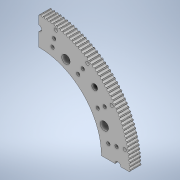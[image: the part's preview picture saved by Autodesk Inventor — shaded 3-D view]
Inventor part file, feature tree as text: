
AUTODESK INVENTOR PART (.ipt)
format: ipt  version: 2020 (Build 240168000, 168)  size: 660,992 bytes
history: native  units: in
note: dims shown in document units (in); Inventor stores cm internally (conversion verified against a paired STEP export)
features: extrude x6, sketch x6, pattern_circular x1
ambient origin geometry x8: Origin, YZ Plane, XZ Plane, XY Plane, X Axis, Y Axis, Z Axis, Center Point
bodies: Solid1 (feature_tree)
feature tree (13):
  extrude  "Extrusion1"  Depth=0.6299in TaperAngle=0.0deg
  extrude  "Extrusion2"  TaperAngle=0.0deg  [1 undecoded]
  pattern_circular  "Circular Pattern1"  Count=176 Angle=360.0deg
  extrude  "Extrusion3"  Depth=4.25in
  extrude  "Extrusion4"  Depth=0.3937in TaperAngle=360.0deg
  extrude  "Extrusion5"  Depth=4.25in
  extrude  "Extrusion6"  Depth=3.1496in TaperAngle=360.0deg
  sketch  "Sketch1"  dims[d0=10.9831in d1=0.6299in d2=0.0in]
  sketch  "Sketch2"  dims[d3=0.0607in d5=0.0in d6=0.0in d7=69.2913in d8=360.0deg]
  sketch  "Sketch3"  dims[d10=0.2031in d11=4.25in]
  sketch  "Sketch4"  dims[d12=1.1811in d14=0.5in d15=0.3937in d17=1.0in d19=6.2992in d21=360.0deg]
  sketch  "Sketch5"  dims[d23=0.5in d24=4.25in]
  sketch  "Sketch6"  dims[d25=0.0773in d26=3.1496in d28=360.0deg d30=4.735in d31=0.35in d33=0.0773in d34=3.1496in d36=360.0deg d38=0.0773in d39=0.0in d40=0.0in d41=7.5in d42=0.0in d43=0.0in d44=0.0in d45=0.0in d47=0.082in d48=0.0098in d49=0.0in]
note: 1 required parameter value undecoded (feature->parameter linkage not recoverable at this tier; creation-order binding heuristic only, values carry confidence <= 0.55)
